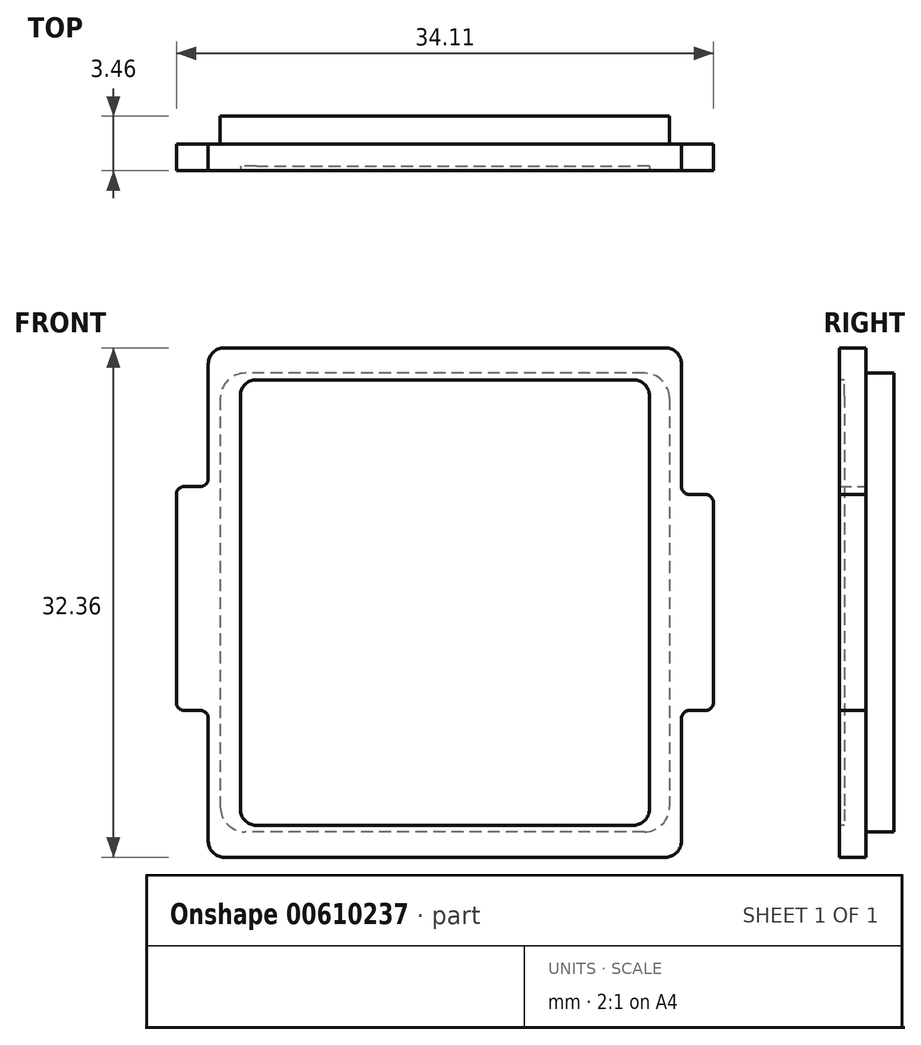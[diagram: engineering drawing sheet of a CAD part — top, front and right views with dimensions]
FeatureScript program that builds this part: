
annotation { "Feature Type Name" : "Feature", "Feature Type Description" : "" }
export const myFeature = defineFeature(function(context is Context, id is Id, definition is map)
    precondition{}
    {
        {
            var Q0;
            Q0=qCreatedBy(makeId("Front.planeOp"),FACE);
            var sketch = newSketch(context, id + "F0", { "sketchPlane" : qUnion([Q0])});
            skLineSegment(sketch, "E0.bottom", {"start": v(1.02, 0) * mm, "end": v(29.03, 0) * mm});
            skLineSegment(sketch, "E0.top", {"start": v(1.02, -32.36) * mm, "end": v(29.03, -32.36) * mm});
            skLineSegment(sketch, "E0.left", {"start": v(0, -1.02) * mm, "end": v(0, -8.3) * mm});
            skLineSegment(sketch, "E0.right", {"start": v(30.05, -1.02) * mm, "end": v(30.05, -8.81) * mm});
            skPoint(sketch, "E1.visualSharp", {"position": v(30.05, 0) * mm});
            skArc(sketch, "E1.filletArc", {"start": v(30.05, -1.02) * mm, "mid": v(29.75, -0.3) * mm, "end": v(29.03, 0) * mm});
            skPoint(sketch, "E2.visualSharp", {"position": v(30.05, -32.36) * mm});
            skArc(sketch, "E2.filletArc", {"start": v(29.03, -32.36) * mm, "mid": v(29.75, -32.06) * mm, "end": v(30.05, -31.34) * mm});
            skPoint(sketch, "E3.visualSharp", {"position": v(0, -32.36) * mm});
            skArc(sketch, "E3.filletArc", {"start": v(0, -31.34) * mm, "mid": v(0.3, -32.06) * mm, "end": v(1.02, -32.36) * mm});
            skPoint(sketch, "E4.visualSharp", {"position": v(0, 0) * mm});
            skArc(sketch, "E4.filletArc", {"start": v(1.02, 0) * mm, "mid": v(0.3, -0.3) * mm, "end": v(0, -1.02) * mm});
            skLineSegment(sketch, "E5.0", {"start": v(32.08, -9.83) * mm, "end": v(32.08, -22.53) * mm});
            skLineSegment(sketch, "E6.0", {"start": v(-2.03, -9.32) * mm, "end": v(-2.03, -22.53) * mm});
            skLineSegment(sketch, "E7", {"start": v(-0.5, -8.81) * mm, "end": v(-1.52, -8.81) * mm});
            skLineSegment(sketch, "E8", {"start": v(-0.5, -23.04) * mm, "end": v(-1.52, -23.04) * mm});
            skLineSegment(sketch, "E9", {"start": v(30.56, -23.04) * mm, "end": v(31.57, -23.04) * mm});
            skLineSegment(sketch, "E10", {"start": v(30.56, -9.32) * mm, "end": v(31.57, -9.32) * mm});
            skLineSegment(sketch, "E11.trimOffspring", {"start": v(30.05, -23.55) * mm, "end": v(30.05, -31.34) * mm});
            skPoint(sketch, "E12.end.orphan", {"position": v(30.05, -16.18) * mm});
            skPoint(sketch, "E12.start.orphan", {"position": v(0, -16.18) * mm});
            skLineSegment(sketch, "E13.trimOffspring", {"start": v(0, -23.55) * mm, "end": v(0, -31.34) * mm});
            skPoint(sketch, "E14.visualSharp", {"position": v(0, -8.81) * mm});
            skArc(sketch, "E14.filletArc", {"start": v(-0.5, -8.81) * mm, "mid": v(-0.15, -8.67) * mm, "end": v(0, -8.3) * mm});
            skPoint(sketch, "E15.visualSharp", {"position": v(-2.03, -8.81) * mm});
            skArc(sketch, "E15.filletArc", {"start": v(-1.52, -8.81) * mm, "mid": v(-1.88, -8.96) * mm, "end": v(-2.03, -9.32) * mm});
            skPoint(sketch, "E16.visualSharp", {"position": v(-2.03, -23.04) * mm});
            skArc(sketch, "E16.filletArc", {"start": v(-2.03, -22.53) * mm, "mid": v(-1.88, -22.89) * mm, "end": v(-1.52, -23.04) * mm});
            skPoint(sketch, "E17.visualSharp", {"position": v(0, -23.04) * mm});
            skArc(sketch, "E17.filletArc", {"start": v(0, -23.55) * mm, "mid": v(-0.15, -23.19) * mm, "end": v(-0.5, -23.04) * mm});
            skPoint(sketch, "E18.visualSharp", {"position": v(30.05, -9.32) * mm});
            skArc(sketch, "E18.filletArc", {"start": v(30.05, -8.81) * mm, "mid": v(30.2, -9.17) * mm, "end": v(30.56, -9.32) * mm});
            skPoint(sketch, "E19.visualSharp", {"position": v(32.08, -9.32) * mm});
            skArc(sketch, "E19.filletArc", {"start": v(32.08, -9.83) * mm, "mid": v(31.93, -9.47) * mm, "end": v(31.57, -9.32) * mm});
            skPoint(sketch, "E20.visualSharp", {"position": v(32.08, -23.04) * mm});
            skArc(sketch, "E20.filletArc", {"start": v(31.57, -23.04) * mm, "mid": v(31.93, -22.89) * mm, "end": v(32.08, -22.53) * mm});
            skPoint(sketch, "E21.visualSharp", {"position": v(30.05, -23.04) * mm});
            skArc(sketch, "E21.filletArc", {"start": v(30.56, -23.04) * mm, "mid": v(30.2, -23.19) * mm, "end": v(30.05, -23.55) * mm});
            skSolve(sketch);
        }
        {
            var Q0;
            Q0 = qSketchRegion(id + "F0", true);
            extrude(context, id + "F1", {"entities" : qUnion([Q0]), "depth" : 1.68 * mm, "offsetDistance" : 25.4 * mm});
        }
        {
            var Q0;
            Q0=makeQuery(id+"F1.opExtrude","CAP_FACE",FACE,{"disambiguationData":[OSD([sQuery(id+"F0.wireOp",EDGE,"E0.bottom"),sQuery(id+"F0.wireOp",EDGE,"E0.top"),sQuery(id+"F0.wireOp",EDGE,"E0.left"),sQuery(id+"F0.wireOp",EDGE,"E0.right")])],"isStart":false});
            var sketch = newSketch(context, id + "F2", { "sketchPlane" : qUnion([Q0])});
            skLineSegment(sketch, "E22.0", {"start": v(3.05, -2.03) * mm, "end": v(27, -2.03) * mm});
            skLineSegment(sketch, "E22.1", {"start": v(2.03, -3.05) * mm, "end": v(2.03, -29.31) * mm});
            skLineSegment(sketch, "E22.2", {"start": v(3.05, -30.33) * mm, "end": v(27, -30.33) * mm});
            skLineSegment(sketch, "E22.3", {"start": v(28.02, -3.05) * mm, "end": v(28.02, -29.31) * mm});
            skPoint(sketch, "E23.visualSharp", {"position": v(2.03, -2.03) * mm});
            skArc(sketch, "E23.filletArc", {"start": v(3.05, -2.03) * mm, "mid": v(2.33, -2.33) * mm, "end": v(2.03, -3.05) * mm});
            skPoint(sketch, "E24.visualSharp", {"position": v(28.02, -2.03) * mm});
            skArc(sketch, "E24.filletArc", {"start": v(28.02, -3.05) * mm, "mid": v(27.72, -2.33) * mm, "end": v(27, -2.03) * mm});
            skPoint(sketch, "E25.visualSharp", {"position": v(28.02, -30.33) * mm});
            skArc(sketch, "E25.filletArc", {"start": v(27, -30.33) * mm, "mid": v(27.72, -30.03) * mm, "end": v(28.02, -29.31) * mm});
            skPoint(sketch, "E26.visualSharp", {"position": v(2.03, -30.33) * mm});
            skArc(sketch, "E26.filletArc", {"start": v(2.03, -29.31) * mm, "mid": v(2.33, -30.03) * mm, "end": v(3.05, -30.33) * mm});
            skSolve(sketch);
        }
        {
            var Q0;
            Q0 = qSketchRegion(id + "F2", true);
            extrude(context, id + "F3", {"entities" : qUnion([Q0]), "operationType" : NewBodyOperationType.REMOVE, "oppositeDirection" : true, "depth" : 0.3 * mm, "offsetDistance" : 25.4 * mm});
        }
        {
            var Q0;
            Q0=makeQuery(id+"F1.opExtrude","CAP_FACE",FACE,{"disambiguationData":[OSD([sQuery(id+"F0.wireOp",EDGE,"E0.bottom"),sQuery(id+"F0.wireOp",EDGE,"E0.top"),sQuery(id+"F0.wireOp",EDGE,"E0.left"),sQuery(id+"F0.wireOp",EDGE,"E0.right"),sQuery(id+"F0.wireOp",EDGE,"E1.filletArc"),sQuery(id+"F0.wireOp",EDGE,"E2.filletArc"),sQuery(id+"F0.wireOp",EDGE,"E3.filletArc"),sQuery(id+"F0.wireOp",EDGE,"E4.filletArc"),sQuery(id+"F0.wireOp",EDGE,"E5.0"),sQuery(id+"F0.wireOp",EDGE,"E6.0"),sQuery(id+"F0.wireOp",EDGE,"E7"),sQuery(id+"F0.wireOp",EDGE,"E8"),sQuery(id+"F0.wireOp",EDGE,"E9"),sQuery(id+"F0.wireOp",EDGE,"E10"),sQuery(id+"F0.wireOp",EDGE,"E11.trimOffspring"),sQuery(id+"F0.wireOp",EDGE,"E13.trimOffspring"),sQuery(id+"F0.wireOp",EDGE,"E14.filletArc"),sQuery(id+"F0.wireOp",EDGE,"E15.filletArc"),sQuery(id+"F0.wireOp",EDGE,"E16.filletArc"),sQuery(id+"F0.wireOp",EDGE,"E17.filletArc"),sQuery(id+"F0.wireOp",EDGE,"E18.filletArc"),sQuery(id+"F0.wireOp",EDGE,"E19.filletArc"),sQuery(id+"F0.wireOp",EDGE,"E20.filletArc"),sQuery(id+"F0.wireOp",EDGE,"E21.filletArc")])],"isStart":true});
            var sketch = newSketch(context, id + "F4", { "sketchPlane" : qUnion([Q0])});
            skLineSegment(sketch, "E27.bottom", {"start": v(-27.7, -1.61) * mm, "end": v(-2.35, -1.61) * mm});
            skLineSegment(sketch, "E27.top", {"start": v(-27.7, -30.75) * mm, "end": v(-2.35, -30.75) * mm});
            skLineSegment(sketch, "E27.left", {"start": v(-29.29, -3.2) * mm, "end": v(-29.29, -29.16) * mm});
            skLineSegment(sketch, "E27.right", {"start": v(-0.76, -3.2) * mm, "end": v(-0.76, -29.16) * mm});
            skPoint(sketch, "E27.middle", {"position": v(-15.02, -16.18) * mm});
            skPoint(sketch, "E27.middle.positionSnap0", {"position": v(-15.02, 0) * mm});
            skPoint(sketch, "E27.middle.positionSnap1", {"position": v(-32.08, -16.18) * mm});
            skPoint(sketch, "E27.centerSnap0", {"position": v(-15.02, 0) * mm});
            skPoint(sketch, "E27.centerSnap1", {"position": v(-32.08, -16.18) * mm});
            skPoint(sketch, "E28.visualSharp", {"position": v(-29.29, -1.61) * mm});
            skArc(sketch, "E28.filletArc", {"start": v(-27.7, -1.61) * mm, "mid": v(-28.82, -2.08) * mm, "end": v(-29.29, -3.2) * mm});
            skPoint(sketch, "E29.visualSharp", {"position": v(-0.76, -1.61) * mm});
            skArc(sketch, "E29.filletArc", {"start": v(-0.76, -3.2) * mm, "mid": v(-1.23, -2.08) * mm, "end": v(-2.35, -1.61) * mm});
            skPoint(sketch, "E30.visualSharp", {"position": v(-0.76, -30.75) * mm});
            skArc(sketch, "E30.filletArc", {"start": v(-2.35, -30.75) * mm, "mid": v(-1.23, -30.28) * mm, "end": v(-0.76, -29.16) * mm});
            skPoint(sketch, "E31.visualSharp", {"position": v(-29.29, -30.75) * mm});
            skArc(sketch, "E31.filletArc", {"start": v(-29.29, -29.16) * mm, "mid": v(-28.82, -30.28) * mm, "end": v(-27.7, -30.75) * mm});
            skSolve(sketch);
        }
        {
            var Q0;
            Q0 = qSketchRegion(id + "F4", true);
            extrude(context, id + "F5", {"entities" : qUnion([Q0]), "operationType" : NewBodyOperationType.ADD, "depth" : 1.78 * mm, "offsetDistance" : 25.4 * mm});
        }
    });
